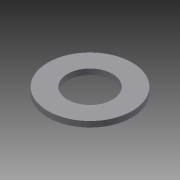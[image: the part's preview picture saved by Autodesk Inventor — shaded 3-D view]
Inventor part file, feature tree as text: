
AUTODESK INVENTOR PART (.ipt)
format: ipt  version: 2014 (Build 180170000, 170)  size: 73,216 bytes
history: native  units: mm
features: extrude x1, sketch x1
ambient origin geometry x8: Origin, YZ Plane, XZ Plane, XY Plane, X Axis, Y Axis, Z Axis, Center Point
bodies: Solid1 (feature_tree)
feature tree (2):
  extrude  "Extrusion1"  Depth=1.0mm
  sketch  "Sketch1"  dims[d0=8.0mm d1=15.0mm d2=1.0mm d3=0.0mm]
